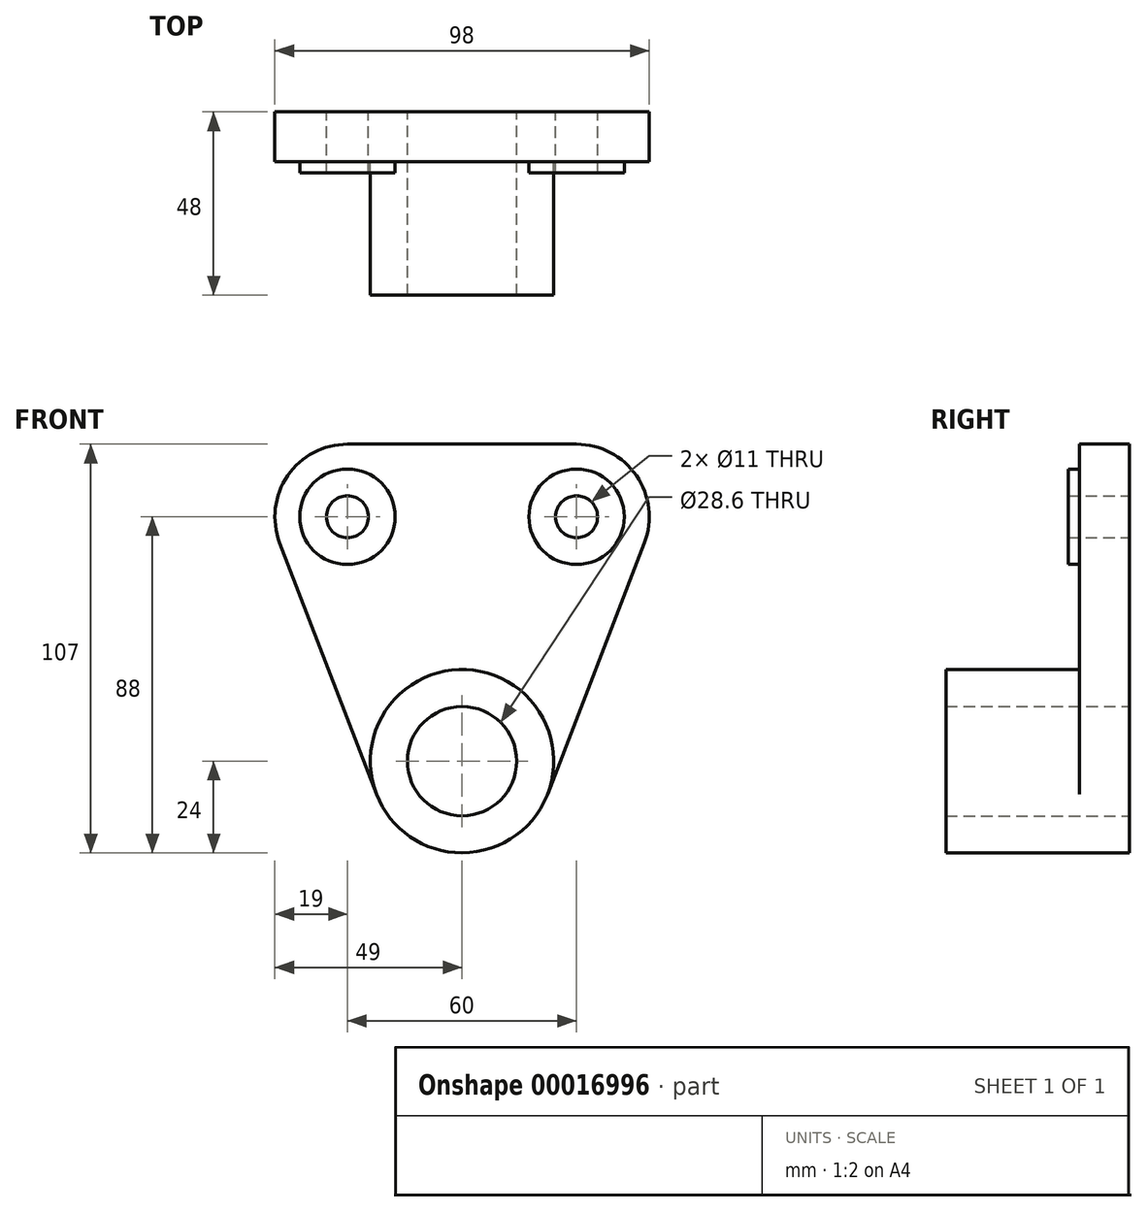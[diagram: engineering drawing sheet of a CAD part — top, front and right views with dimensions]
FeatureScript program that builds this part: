
annotation { "Feature Type Name" : "Feature", "Feature Type Description" : "" }
export const myFeature = defineFeature(function(context is Context, id is Id, definition is map)
    precondition{}
    {
        {
            var Q0;
            Q0=qCreatedBy(makeId("Front.planeOp"),FACE);
            var sketch = newSketch(context, id + "F0", { "sketchPlane" : qUnion([Q0])});
            skArc(sketch, "E0", {"start": v(-30, 49.04) * mm, "mid": v(-45.66, 40.8) * mm, "end": v(-47.73, 23.21) * mm});
            skCircle(sketch, "E1", {"center": v(-30, 30.04) * mm, "radius": 12.5 * mm});
            skArc(sketch, "E2", {"start": v(47.73, 23.21) * mm, "mid": v(45.66, 40.8) * mm, "end": v(30, 49.04) * mm});
            skCircle(sketch, "E3", {"center": v(30, 30.04) * mm, "radius": 12.5 * mm});
            skCircle(sketch, "E4", {"center": v(0, -33.96) * mm, "radius": 24 * mm});
            skCircle(sketch, "E5", {"center": v(0, -33.96) * mm, "radius": 14.3 * mm});
            skLineSegment(sketch, "E6", {"start": v(-30, 49.04) * mm, "end": v(30, 49.04) * mm});
            skLineSegment(sketch, "E7", {"start": v(-22.4, -42.58) * mm, "end": v(-47.73, 23.21) * mm});
            skLineSegment(sketch, "E8", {"start": v(22.4, -42.58) * mm, "end": v(47.73, 23.21) * mm});
            skCircle(sketch, "E9", {"center": v(-30, 30.04) * mm, "radius": 5.5 * mm});
            skCircle(sketch, "E10", {"center": v(30, 30.04) * mm, "radius": 5.5 * mm});
            skSolve(sketch);
        }
        {
            var Q0;
            Q0 = qSketchRegion(id + "F0", true);
            extrude(context, id + "F1", {"entities" : qUnion([Q0]), "depth" : 13 * mm});
        }
        {
            var Q0;
            Q0=makeQuery(id+"F0.imprint","IMPRINT",FACE,{"disambiguationData":[TD([[makeQuery(id+"F0.imprint","IMPRINT",EDGE,{"derivedFrom":sQuery(id+"F0.wireOp",EDGE,"E3")}),1.0]])]});
            var Q1;
            Q1=makeQuery(id+"F0.imprint","IMPRINT",FACE,{"disambiguationData":[TD([[makeQuery(id+"F0.imprint","IMPRINT",EDGE,{"derivedFrom":sQuery(id+"F0.wireOp",EDGE,"E1")}),1.0]])]});
            extrude(context, id + "F2", {"entities" : qUnion([Q0, Q1]), "operationType" : NewBodyOperationType.ADD, "depth" : 16 * mm});
        }
        {
            var Q0;
            Q0=makeQuery(id+"F0.imprint","IMPRINT",FACE,{"disambiguationData":[TD([[makeQuery(id+"F0.imprint","IMPRINT",EDGE,{"derivedFrom":sQuery(id+"F0.wireOp",EDGE,"E5")}),-1.0]])]});
            extrude(context, id + "F3", {"entities" : qUnion([Q0]), "operationType" : NewBodyOperationType.ADD, "depth" : 48 * mm});
        }
    });
